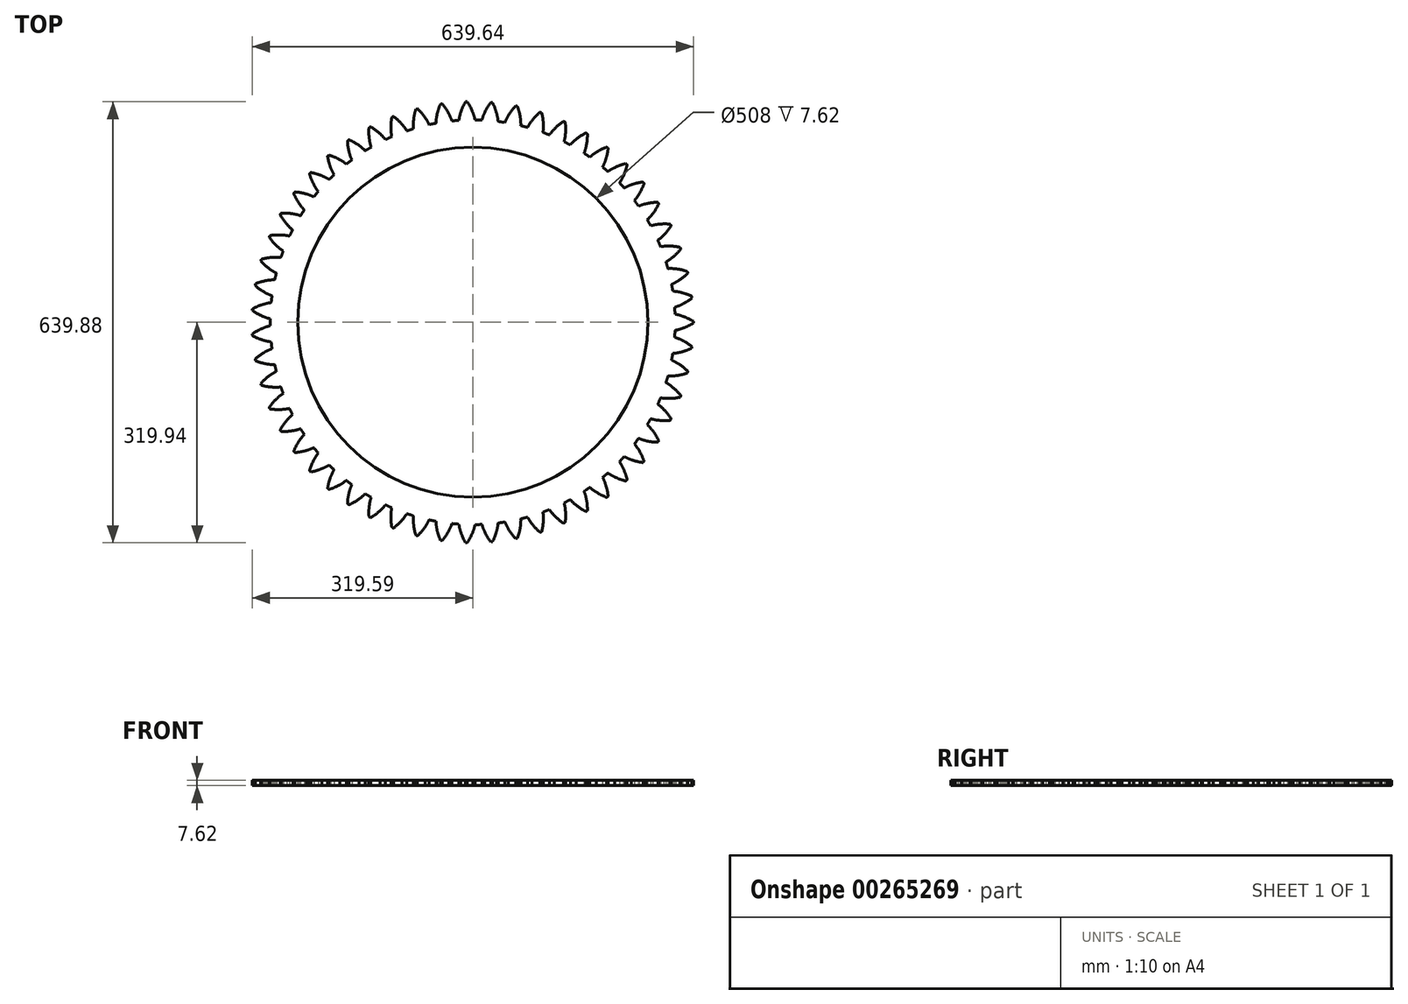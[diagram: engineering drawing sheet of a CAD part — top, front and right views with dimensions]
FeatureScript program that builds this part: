
annotation { "Feature Type Name" : "Feature", "Feature Type Description" : "" }
export const myFeature = defineFeature(function(context is Context, id is Id, definition is map)
    precondition{}
    {
        {
            var Q0;
            Q0=qCreatedBy(makeId("Top.planeOp"),FACE);
            var sketch = newSketch(context, id + "F0", { "sketchPlane" : qUnion([Q0])});
            skCircle(sketch, "E0", {"center": v(0, 0) * mm, "radius": 293.72 * mm});
            skCircle(sketch, "E1", {"center": v(0, 0) * mm, "radius": 304.8 * mm, "construction": true});
            skCircle(sketch, "E2", {"center": v(0, 0) * mm, "radius": 320.04 * mm, "construction": true});
            skLineSegment(sketch, "E3", {"start": v(0, 0) * mm, "end": v(0, 420.14) * mm, "construction": true});
            skLineSegment(sketch, "E4", {"start": v(0, 0) * mm, "end": v(-11.66, 408.27) * mm, "construction": true});
            skLineSegment(sketch, "E5", {"start": v(0, 304.8) * mm, "end": v(-381.83, 304.8) * mm, "construction": true});
            skLineSegment(sketch, "E6", {"start": v(0, 304.8) * mm, "end": v(-397.99, 159.94) * mm, "construction": true});
            skCircle(sketch, "E7", {"center": v(0, 0) * mm, "radius": 286.42 * mm, "construction": true});
            skCircle(sketch, "E8", {"center": v(0, 304.8) * mm, "radius": 76.2 * mm, "construction": true});
            skCircle(sketch, "E9", {"center": v(-71.12, 277.45) * mm, "radius": 76.2 * mm, "construction": true});
            skArc(sketch, "E10", {"start": v(-7.87, 319.94) * mm, "mid": v(-9.14, 319.92) * mm, "end": v(-10.4, 319.87) * mm});
            skArc(sketch, "E11", {"start": v(0, 304.8) * mm, "mid": v(-3.5, 312.6) * mm, "end": v(-7.87, 319.94) * mm});
            skArc(sketch, "E12.MirrorCS", {"start": v(-17.4, 304.3) * mm, "mid": v(-14.35, 312.29) * mm, "end": v(-10.4, 319.87) * mm});
            skArc(sketch, "E13", {"start": v(-17.4, 304.3) * mm, "mid": v(-19.02, 298.73) * mm, "end": v(-20.09, 293.03) * mm});
            skArc(sketch, "E14.MirrorCS", {"start": v(0, 304.8) * mm, "mid": v(1.94, 299.33) * mm, "end": v(3.33, 293.7) * mm});
            skSolve(sketch);
        }
        {
            var Q0;
            Q0=qSketchRegion(id+"F0",true);
            extrude(context, id + "F1", {"entities" : qUnion([Q0]), "depth" : 7.62 * mm});
        }
        {
            var Q0;
            Q0=makeQuery(id+"F1.opExtrude","SWEPT_BODY",BODY,{"disambiguationData":[OSD([sQuery(id+"F0.wireOp",EDGE,"E0"),sQuery(id+"F0.wireOp",EDGE,"91NiUCr4-yXFt-oEsC-2t8w-iLQuIMEs0WGp"),sQuery(id+"F0.wireOp",EDGE,"2eccd6a7-b62e-4e30-96b3-c5b5e07e5a5b0.MirrorCS"),sQuery(id+"F0.wireOp",EDGE,"E10")])]});
            var Q1;
            Q1=makeQuery(id+"F1.opExtrude","SWEPT_FACE",FACE,{"disambiguationData":[OSD([sQuery(id+"F0.wireOp",EDGE,"E0")])]});
            circularPattern(context, id + "F2", {"entities" : qUnion([Q0]), "axis" : qUnion([Q1]), "angle" : 360 * degree, "instanceCount" : 55, "equalSpace" : true});
        }
        {
            var Q0;
            Q0=makeQuery(id+"F1.opExtrude","SWEPT_BODY",BODY,{"disambiguationData":[OSD([sQuery(id+"F0.wireOp",EDGE,"E0"),sQuery(id+"F0.wireOp",EDGE,"E10"),sQuery(id+"F0.wireOp",EDGE,"E11"),sQuery(id+"F0.wireOp",EDGE,"E12.MirrorCS"),sQuery(id+"F0.wireOp",EDGE,"E13"),sQuery(id+"F0.wireOp",EDGE,"E14.MirrorCS")])]});
            var Q1;
            Q1=makeQuery(id+"F2.opPattern","COPY",BODY,{"derivedFrom":makeQuery(id+"F1.opExtrude","SWEPT_BODY",BODY,{"disambiguationData":[OSD([sQuery(id+"F0.wireOp",EDGE,"E0"),sQuery(id+"F0.wireOp",EDGE,"E10"),sQuery(id+"F0.wireOp",EDGE,"E11"),sQuery(id+"F0.wireOp",EDGE,"E12.MirrorCS"),sQuery(id+"F0.wireOp",EDGE,"E13"),sQuery(id+"F0.wireOp",EDGE,"E14.MirrorCS")])]}),"instanceName":"1"});
            var Q2;
            Q2=makeQuery(id+"F2.opPattern","COPY",BODY,{"derivedFrom":makeQuery(id+"F1.opExtrude","SWEPT_BODY",BODY,{"disambiguationData":[OSD([sQuery(id+"F0.wireOp",EDGE,"E0"),sQuery(id+"F0.wireOp",EDGE,"E10"),sQuery(id+"F0.wireOp",EDGE,"E11"),sQuery(id+"F0.wireOp",EDGE,"E12.MirrorCS"),sQuery(id+"F0.wireOp",EDGE,"E13"),sQuery(id+"F0.wireOp",EDGE,"E14.MirrorCS")])]}),"instanceName":"2"});
            var Q3;
            Q3=makeQuery(id+"F2.opPattern","COPY",BODY,{"derivedFrom":makeQuery(id+"F1.opExtrude","SWEPT_BODY",BODY,{"disambiguationData":[OSD([sQuery(id+"F0.wireOp",EDGE,"E0"),sQuery(id+"F0.wireOp",EDGE,"E10"),sQuery(id+"F0.wireOp",EDGE,"E11"),sQuery(id+"F0.wireOp",EDGE,"E12.MirrorCS"),sQuery(id+"F0.wireOp",EDGE,"E13"),sQuery(id+"F0.wireOp",EDGE,"E14.MirrorCS")])]}),"instanceName":"3"});
            var Q4;
            Q4=makeQuery(id+"F2.opPattern","COPY",BODY,{"derivedFrom":makeQuery(id+"F1.opExtrude","SWEPT_BODY",BODY,{"disambiguationData":[OSD([sQuery(id+"F0.wireOp",EDGE,"E0"),sQuery(id+"F0.wireOp",EDGE,"E10"),sQuery(id+"F0.wireOp",EDGE,"E11"),sQuery(id+"F0.wireOp",EDGE,"E12.MirrorCS"),sQuery(id+"F0.wireOp",EDGE,"E13"),sQuery(id+"F0.wireOp",EDGE,"E14.MirrorCS")])]}),"instanceName":"4"});
            var Q5;
            Q5=makeQuery(id+"F2.opPattern","COPY",BODY,{"derivedFrom":makeQuery(id+"F1.opExtrude","SWEPT_BODY",BODY,{"disambiguationData":[OSD([sQuery(id+"F0.wireOp",EDGE,"E0"),sQuery(id+"F0.wireOp",EDGE,"E10"),sQuery(id+"F0.wireOp",EDGE,"E11"),sQuery(id+"F0.wireOp",EDGE,"E12.MirrorCS"),sQuery(id+"F0.wireOp",EDGE,"E13"),sQuery(id+"F0.wireOp",EDGE,"E14.MirrorCS")])]}),"instanceName":"5"});
            var Q6;
            Q6=makeQuery(id+"F2.opPattern","COPY",BODY,{"derivedFrom":makeQuery(id+"F1.opExtrude","SWEPT_BODY",BODY,{"disambiguationData":[OSD([sQuery(id+"F0.wireOp",EDGE,"E0"),sQuery(id+"F0.wireOp",EDGE,"E10"),sQuery(id+"F0.wireOp",EDGE,"E11"),sQuery(id+"F0.wireOp",EDGE,"E12.MirrorCS"),sQuery(id+"F0.wireOp",EDGE,"E13"),sQuery(id+"F0.wireOp",EDGE,"E14.MirrorCS")])]}),"instanceName":"6"});
            var Q7;
            Q7=makeQuery(id+"F2.opPattern","COPY",BODY,{"derivedFrom":makeQuery(id+"F1.opExtrude","SWEPT_BODY",BODY,{"disambiguationData":[OSD([sQuery(id+"F0.wireOp",EDGE,"E0"),sQuery(id+"F0.wireOp",EDGE,"E10"),sQuery(id+"F0.wireOp",EDGE,"E11"),sQuery(id+"F0.wireOp",EDGE,"E12.MirrorCS"),sQuery(id+"F0.wireOp",EDGE,"E13"),sQuery(id+"F0.wireOp",EDGE,"E14.MirrorCS")])]}),"instanceName":"7"});
            var Q8;
            Q8=makeQuery(id+"F2.opPattern","COPY",BODY,{"derivedFrom":makeQuery(id+"F1.opExtrude","SWEPT_BODY",BODY,{"disambiguationData":[OSD([sQuery(id+"F0.wireOp",EDGE,"E0"),sQuery(id+"F0.wireOp",EDGE,"E10"),sQuery(id+"F0.wireOp",EDGE,"E11"),sQuery(id+"F0.wireOp",EDGE,"E12.MirrorCS"),sQuery(id+"F0.wireOp",EDGE,"E13"),sQuery(id+"F0.wireOp",EDGE,"E14.MirrorCS")])]}),"instanceName":"8"});
            var Q9;
            Q9=makeQuery(id+"F2.opPattern","COPY",BODY,{"derivedFrom":makeQuery(id+"F1.opExtrude","SWEPT_BODY",BODY,{"disambiguationData":[OSD([sQuery(id+"F0.wireOp",EDGE,"E0"),sQuery(id+"F0.wireOp",EDGE,"E10"),sQuery(id+"F0.wireOp",EDGE,"E11"),sQuery(id+"F0.wireOp",EDGE,"E12.MirrorCS"),sQuery(id+"F0.wireOp",EDGE,"E13"),sQuery(id+"F0.wireOp",EDGE,"E14.MirrorCS")])]}),"instanceName":"9"});
            var Q10;
            Q10=makeQuery(id+"F2.opPattern","COPY",BODY,{"derivedFrom":makeQuery(id+"F1.opExtrude","SWEPT_BODY",BODY,{"disambiguationData":[OSD([sQuery(id+"F0.wireOp",EDGE,"E0"),sQuery(id+"F0.wireOp",EDGE,"E10"),sQuery(id+"F0.wireOp",EDGE,"E11"),sQuery(id+"F0.wireOp",EDGE,"E12.MirrorCS"),sQuery(id+"F0.wireOp",EDGE,"E13"),sQuery(id+"F0.wireOp",EDGE,"E14.MirrorCS")])]}),"instanceName":"10"});
            var Q11;
            Q11=makeQuery(id+"F2.opPattern","COPY",BODY,{"derivedFrom":makeQuery(id+"F1.opExtrude","SWEPT_BODY",BODY,{"disambiguationData":[OSD([sQuery(id+"F0.wireOp",EDGE,"E0"),sQuery(id+"F0.wireOp",EDGE,"E10"),sQuery(id+"F0.wireOp",EDGE,"E11"),sQuery(id+"F0.wireOp",EDGE,"E12.MirrorCS"),sQuery(id+"F0.wireOp",EDGE,"E13"),sQuery(id+"F0.wireOp",EDGE,"E14.MirrorCS")])]}),"instanceName":"11"});
            var Q12;
            Q12=makeQuery(id+"F2.opPattern","COPY",BODY,{"derivedFrom":makeQuery(id+"F1.opExtrude","SWEPT_BODY",BODY,{"disambiguationData":[OSD([sQuery(id+"F0.wireOp",EDGE,"E0"),sQuery(id+"F0.wireOp",EDGE,"E10"),sQuery(id+"F0.wireOp",EDGE,"E11"),sQuery(id+"F0.wireOp",EDGE,"E12.MirrorCS"),sQuery(id+"F0.wireOp",EDGE,"E13"),sQuery(id+"F0.wireOp",EDGE,"E14.MirrorCS")])]}),"instanceName":"12"});
            var Q13;
            Q13=makeQuery(id+"F2.opPattern","COPY",BODY,{"derivedFrom":makeQuery(id+"F1.opExtrude","SWEPT_BODY",BODY,{"disambiguationData":[OSD([sQuery(id+"F0.wireOp",EDGE,"E0"),sQuery(id+"F0.wireOp",EDGE,"E10"),sQuery(id+"F0.wireOp",EDGE,"E11"),sQuery(id+"F0.wireOp",EDGE,"E12.MirrorCS"),sQuery(id+"F0.wireOp",EDGE,"E13"),sQuery(id+"F0.wireOp",EDGE,"E14.MirrorCS")])]}),"instanceName":"13"});
            var Q14;
            Q14=makeQuery(id+"F2.opPattern","COPY",BODY,{"derivedFrom":makeQuery(id+"F1.opExtrude","SWEPT_BODY",BODY,{"disambiguationData":[OSD([sQuery(id+"F0.wireOp",EDGE,"E0"),sQuery(id+"F0.wireOp",EDGE,"E10"),sQuery(id+"F0.wireOp",EDGE,"E11"),sQuery(id+"F0.wireOp",EDGE,"E12.MirrorCS"),sQuery(id+"F0.wireOp",EDGE,"E13"),sQuery(id+"F0.wireOp",EDGE,"E14.MirrorCS")])]}),"instanceName":"14"});
            var Q15;
            Q15=makeQuery(id+"F2.opPattern","COPY",BODY,{"derivedFrom":makeQuery(id+"F1.opExtrude","SWEPT_BODY",BODY,{"disambiguationData":[OSD([sQuery(id+"F0.wireOp",EDGE,"E0"),sQuery(id+"F0.wireOp",EDGE,"E10"),sQuery(id+"F0.wireOp",EDGE,"E11"),sQuery(id+"F0.wireOp",EDGE,"E12.MirrorCS"),sQuery(id+"F0.wireOp",EDGE,"E13"),sQuery(id+"F0.wireOp",EDGE,"E14.MirrorCS")])]}),"instanceName":"15"});
            var Q16;
            Q16=makeQuery(id+"F2.opPattern","COPY",BODY,{"derivedFrom":makeQuery(id+"F1.opExtrude","SWEPT_BODY",BODY,{"disambiguationData":[OSD([sQuery(id+"F0.wireOp",EDGE,"E0"),sQuery(id+"F0.wireOp",EDGE,"E10"),sQuery(id+"F0.wireOp",EDGE,"E11"),sQuery(id+"F0.wireOp",EDGE,"E12.MirrorCS"),sQuery(id+"F0.wireOp",EDGE,"E13"),sQuery(id+"F0.wireOp",EDGE,"E14.MirrorCS")])]}),"instanceName":"16"});
            var Q17;
            Q17=makeQuery(id+"F2.opPattern","COPY",BODY,{"derivedFrom":makeQuery(id+"F1.opExtrude","SWEPT_BODY",BODY,{"disambiguationData":[OSD([sQuery(id+"F0.wireOp",EDGE,"E0"),sQuery(id+"F0.wireOp",EDGE,"E10"),sQuery(id+"F0.wireOp",EDGE,"E11"),sQuery(id+"F0.wireOp",EDGE,"E12.MirrorCS"),sQuery(id+"F0.wireOp",EDGE,"E13"),sQuery(id+"F0.wireOp",EDGE,"E14.MirrorCS")])]}),"instanceName":"17"});
            var Q18;
            Q18=makeQuery(id+"F2.opPattern","COPY",BODY,{"derivedFrom":makeQuery(id+"F1.opExtrude","SWEPT_BODY",BODY,{"disambiguationData":[OSD([sQuery(id+"F0.wireOp",EDGE,"E0"),sQuery(id+"F0.wireOp",EDGE,"E10"),sQuery(id+"F0.wireOp",EDGE,"E11"),sQuery(id+"F0.wireOp",EDGE,"E12.MirrorCS"),sQuery(id+"F0.wireOp",EDGE,"E13"),sQuery(id+"F0.wireOp",EDGE,"E14.MirrorCS")])]}),"instanceName":"18"});
            var Q19;
            Q19=makeQuery(id+"F2.opPattern","COPY",BODY,{"derivedFrom":makeQuery(id+"F1.opExtrude","SWEPT_BODY",BODY,{"disambiguationData":[OSD([sQuery(id+"F0.wireOp",EDGE,"E0"),sQuery(id+"F0.wireOp",EDGE,"E10"),sQuery(id+"F0.wireOp",EDGE,"E11"),sQuery(id+"F0.wireOp",EDGE,"E12.MirrorCS"),sQuery(id+"F0.wireOp",EDGE,"E13"),sQuery(id+"F0.wireOp",EDGE,"E14.MirrorCS")])]}),"instanceName":"19"});
            var Q20;
            Q20=makeQuery(id+"F2.opPattern","COPY",BODY,{"derivedFrom":makeQuery(id+"F1.opExtrude","SWEPT_BODY",BODY,{"disambiguationData":[OSD([sQuery(id+"F0.wireOp",EDGE,"E0"),sQuery(id+"F0.wireOp",EDGE,"E10"),sQuery(id+"F0.wireOp",EDGE,"E11"),sQuery(id+"F0.wireOp",EDGE,"E12.MirrorCS"),sQuery(id+"F0.wireOp",EDGE,"E13"),sQuery(id+"F0.wireOp",EDGE,"E14.MirrorCS")])]}),"instanceName":"20"});
            var Q21;
            Q21=makeQuery(id+"F2.opPattern","COPY",BODY,{"derivedFrom":makeQuery(id+"F1.opExtrude","SWEPT_BODY",BODY,{"disambiguationData":[OSD([sQuery(id+"F0.wireOp",EDGE,"E0"),sQuery(id+"F0.wireOp",EDGE,"E10"),sQuery(id+"F0.wireOp",EDGE,"E11"),sQuery(id+"F0.wireOp",EDGE,"E12.MirrorCS"),sQuery(id+"F0.wireOp",EDGE,"E13"),sQuery(id+"F0.wireOp",EDGE,"E14.MirrorCS")])]}),"instanceName":"21"});
            var Q22;
            Q22=makeQuery(id+"F2.opPattern","COPY",BODY,{"derivedFrom":makeQuery(id+"F1.opExtrude","SWEPT_BODY",BODY,{"disambiguationData":[OSD([sQuery(id+"F0.wireOp",EDGE,"E0"),sQuery(id+"F0.wireOp",EDGE,"E10"),sQuery(id+"F0.wireOp",EDGE,"E11"),sQuery(id+"F0.wireOp",EDGE,"E12.MirrorCS"),sQuery(id+"F0.wireOp",EDGE,"E13"),sQuery(id+"F0.wireOp",EDGE,"E14.MirrorCS")])]}),"instanceName":"22"});
            var Q23;
            Q23=makeQuery(id+"F2.opPattern","COPY",BODY,{"derivedFrom":makeQuery(id+"F1.opExtrude","SWEPT_BODY",BODY,{"disambiguationData":[OSD([sQuery(id+"F0.wireOp",EDGE,"E0"),sQuery(id+"F0.wireOp",EDGE,"E10"),sQuery(id+"F0.wireOp",EDGE,"E11"),sQuery(id+"F0.wireOp",EDGE,"E12.MirrorCS"),sQuery(id+"F0.wireOp",EDGE,"E13"),sQuery(id+"F0.wireOp",EDGE,"E14.MirrorCS")])]}),"instanceName":"23"});
            var Q24;
            Q24=makeQuery(id+"F2.opPattern","COPY",BODY,{"derivedFrom":makeQuery(id+"F1.opExtrude","SWEPT_BODY",BODY,{"disambiguationData":[OSD([sQuery(id+"F0.wireOp",EDGE,"E0"),sQuery(id+"F0.wireOp",EDGE,"E10"),sQuery(id+"F0.wireOp",EDGE,"E11"),sQuery(id+"F0.wireOp",EDGE,"E12.MirrorCS"),sQuery(id+"F0.wireOp",EDGE,"E13"),sQuery(id+"F0.wireOp",EDGE,"E14.MirrorCS")])]}),"instanceName":"24"});
            var Q25;
            Q25=makeQuery(id+"F2.opPattern","COPY",BODY,{"derivedFrom":makeQuery(id+"F1.opExtrude","SWEPT_BODY",BODY,{"disambiguationData":[OSD([sQuery(id+"F0.wireOp",EDGE,"E0"),sQuery(id+"F0.wireOp",EDGE,"E10"),sQuery(id+"F0.wireOp",EDGE,"E11"),sQuery(id+"F0.wireOp",EDGE,"E12.MirrorCS"),sQuery(id+"F0.wireOp",EDGE,"E13"),sQuery(id+"F0.wireOp",EDGE,"E14.MirrorCS")])]}),"instanceName":"25"});
            var Q26;
            Q26=makeQuery(id+"F2.opPattern","COPY",BODY,{"derivedFrom":makeQuery(id+"F1.opExtrude","SWEPT_BODY",BODY,{"disambiguationData":[OSD([sQuery(id+"F0.wireOp",EDGE,"E0"),sQuery(id+"F0.wireOp",EDGE,"E10"),sQuery(id+"F0.wireOp",EDGE,"E11"),sQuery(id+"F0.wireOp",EDGE,"E12.MirrorCS"),sQuery(id+"F0.wireOp",EDGE,"E13"),sQuery(id+"F0.wireOp",EDGE,"E14.MirrorCS")])]}),"instanceName":"26"});
            var Q27;
            Q27=makeQuery(id+"F2.opPattern","COPY",BODY,{"derivedFrom":makeQuery(id+"F1.opExtrude","SWEPT_BODY",BODY,{"disambiguationData":[OSD([sQuery(id+"F0.wireOp",EDGE,"E0"),sQuery(id+"F0.wireOp",EDGE,"E10"),sQuery(id+"F0.wireOp",EDGE,"E11"),sQuery(id+"F0.wireOp",EDGE,"E12.MirrorCS"),sQuery(id+"F0.wireOp",EDGE,"E13"),sQuery(id+"F0.wireOp",EDGE,"E14.MirrorCS")])]}),"instanceName":"27"});
            var Q28;
            Q28=makeQuery(id+"F2.opPattern","COPY",BODY,{"derivedFrom":makeQuery(id+"F1.opExtrude","SWEPT_BODY",BODY,{"disambiguationData":[OSD([sQuery(id+"F0.wireOp",EDGE,"E0"),sQuery(id+"F0.wireOp",EDGE,"E10"),sQuery(id+"F0.wireOp",EDGE,"E11"),sQuery(id+"F0.wireOp",EDGE,"E12.MirrorCS"),sQuery(id+"F0.wireOp",EDGE,"E13"),sQuery(id+"F0.wireOp",EDGE,"E14.MirrorCS")])]}),"instanceName":"28"});
            var Q29;
            Q29=makeQuery(id+"F2.opPattern","COPY",BODY,{"derivedFrom":makeQuery(id+"F1.opExtrude","SWEPT_BODY",BODY,{"disambiguationData":[OSD([sQuery(id+"F0.wireOp",EDGE,"E0"),sQuery(id+"F0.wireOp",EDGE,"E10"),sQuery(id+"F0.wireOp",EDGE,"E11"),sQuery(id+"F0.wireOp",EDGE,"E12.MirrorCS"),sQuery(id+"F0.wireOp",EDGE,"E13"),sQuery(id+"F0.wireOp",EDGE,"E14.MirrorCS")])]}),"instanceName":"29"});
            var Q30;
            Q30=makeQuery(id+"F2.opPattern","COPY",BODY,{"derivedFrom":makeQuery(id+"F1.opExtrude","SWEPT_BODY",BODY,{"disambiguationData":[OSD([sQuery(id+"F0.wireOp",EDGE,"E0"),sQuery(id+"F0.wireOp",EDGE,"E10"),sQuery(id+"F0.wireOp",EDGE,"E11"),sQuery(id+"F0.wireOp",EDGE,"E12.MirrorCS"),sQuery(id+"F0.wireOp",EDGE,"E13"),sQuery(id+"F0.wireOp",EDGE,"E14.MirrorCS")])]}),"instanceName":"30"});
            var Q31;
            Q31=makeQuery(id+"F2.opPattern","COPY",BODY,{"derivedFrom":makeQuery(id+"F1.opExtrude","SWEPT_BODY",BODY,{"disambiguationData":[OSD([sQuery(id+"F0.wireOp",EDGE,"E0"),sQuery(id+"F0.wireOp",EDGE,"E10"),sQuery(id+"F0.wireOp",EDGE,"E11"),sQuery(id+"F0.wireOp",EDGE,"E12.MirrorCS"),sQuery(id+"F0.wireOp",EDGE,"E13"),sQuery(id+"F0.wireOp",EDGE,"E14.MirrorCS")])]}),"instanceName":"31"});
            var Q32;
            Q32=makeQuery(id+"F2.opPattern","COPY",BODY,{"derivedFrom":makeQuery(id+"F1.opExtrude","SWEPT_BODY",BODY,{"disambiguationData":[OSD([sQuery(id+"F0.wireOp",EDGE,"E0"),sQuery(id+"F0.wireOp",EDGE,"E10"),sQuery(id+"F0.wireOp",EDGE,"E11"),sQuery(id+"F0.wireOp",EDGE,"E12.MirrorCS"),sQuery(id+"F0.wireOp",EDGE,"E13"),sQuery(id+"F0.wireOp",EDGE,"E14.MirrorCS")])]}),"instanceName":"32"});
            var Q33;
            Q33=makeQuery(id+"F2.opPattern","COPY",BODY,{"derivedFrom":makeQuery(id+"F1.opExtrude","SWEPT_BODY",BODY,{"disambiguationData":[OSD([sQuery(id+"F0.wireOp",EDGE,"E0"),sQuery(id+"F0.wireOp",EDGE,"E10"),sQuery(id+"F0.wireOp",EDGE,"E11"),sQuery(id+"F0.wireOp",EDGE,"E12.MirrorCS"),sQuery(id+"F0.wireOp",EDGE,"E13"),sQuery(id+"F0.wireOp",EDGE,"E14.MirrorCS")])]}),"instanceName":"33"});
            var Q34;
            Q34=makeQuery(id+"F2.opPattern","COPY",BODY,{"derivedFrom":makeQuery(id+"F1.opExtrude","SWEPT_BODY",BODY,{"disambiguationData":[OSD([sQuery(id+"F0.wireOp",EDGE,"E0"),sQuery(id+"F0.wireOp",EDGE,"E10"),sQuery(id+"F0.wireOp",EDGE,"E11"),sQuery(id+"F0.wireOp",EDGE,"E12.MirrorCS"),sQuery(id+"F0.wireOp",EDGE,"E13"),sQuery(id+"F0.wireOp",EDGE,"E14.MirrorCS")])]}),"instanceName":"34"});
            var Q35;
            Q35=makeQuery(id+"F2.opPattern","COPY",BODY,{"derivedFrom":makeQuery(id+"F1.opExtrude","SWEPT_BODY",BODY,{"disambiguationData":[OSD([sQuery(id+"F0.wireOp",EDGE,"E0"),sQuery(id+"F0.wireOp",EDGE,"E10"),sQuery(id+"F0.wireOp",EDGE,"E11"),sQuery(id+"F0.wireOp",EDGE,"E12.MirrorCS"),sQuery(id+"F0.wireOp",EDGE,"E13"),sQuery(id+"F0.wireOp",EDGE,"E14.MirrorCS")])]}),"instanceName":"35"});
            var Q36;
            Q36=makeQuery(id+"F2.opPattern","COPY",BODY,{"derivedFrom":makeQuery(id+"F1.opExtrude","SWEPT_BODY",BODY,{"disambiguationData":[OSD([sQuery(id+"F0.wireOp",EDGE,"E0"),sQuery(id+"F0.wireOp",EDGE,"E10"),sQuery(id+"F0.wireOp",EDGE,"E11"),sQuery(id+"F0.wireOp",EDGE,"E12.MirrorCS"),sQuery(id+"F0.wireOp",EDGE,"E13"),sQuery(id+"F0.wireOp",EDGE,"E14.MirrorCS")])]}),"instanceName":"36"});
            var Q37;
            Q37=makeQuery(id+"F2.opPattern","COPY",BODY,{"derivedFrom":makeQuery(id+"F1.opExtrude","SWEPT_BODY",BODY,{"disambiguationData":[OSD([sQuery(id+"F0.wireOp",EDGE,"E0"),sQuery(id+"F0.wireOp",EDGE,"E10"),sQuery(id+"F0.wireOp",EDGE,"E11"),sQuery(id+"F0.wireOp",EDGE,"E12.MirrorCS"),sQuery(id+"F0.wireOp",EDGE,"E13"),sQuery(id+"F0.wireOp",EDGE,"E14.MirrorCS")])]}),"instanceName":"37"});
            var Q38;
            Q38=makeQuery(id+"F2.opPattern","COPY",BODY,{"derivedFrom":makeQuery(id+"F1.opExtrude","SWEPT_BODY",BODY,{"disambiguationData":[OSD([sQuery(id+"F0.wireOp",EDGE,"E0"),sQuery(id+"F0.wireOp",EDGE,"E10"),sQuery(id+"F0.wireOp",EDGE,"E11"),sQuery(id+"F0.wireOp",EDGE,"E12.MirrorCS"),sQuery(id+"F0.wireOp",EDGE,"E13"),sQuery(id+"F0.wireOp",EDGE,"E14.MirrorCS")])]}),"instanceName":"38"});
            var Q39;
            Q39=makeQuery(id+"F2.opPattern","COPY",BODY,{"derivedFrom":makeQuery(id+"F1.opExtrude","SWEPT_BODY",BODY,{"disambiguationData":[OSD([sQuery(id+"F0.wireOp",EDGE,"E0"),sQuery(id+"F0.wireOp",EDGE,"E10"),sQuery(id+"F0.wireOp",EDGE,"E11"),sQuery(id+"F0.wireOp",EDGE,"E12.MirrorCS"),sQuery(id+"F0.wireOp",EDGE,"E13"),sQuery(id+"F0.wireOp",EDGE,"E14.MirrorCS")])]}),"instanceName":"39"});
            var Q40;
            Q40=makeQuery(id+"F2.opPattern","COPY",BODY,{"derivedFrom":makeQuery(id+"F1.opExtrude","SWEPT_BODY",BODY,{"disambiguationData":[OSD([sQuery(id+"F0.wireOp",EDGE,"E0"),sQuery(id+"F0.wireOp",EDGE,"E10"),sQuery(id+"F0.wireOp",EDGE,"E11"),sQuery(id+"F0.wireOp",EDGE,"E12.MirrorCS"),sQuery(id+"F0.wireOp",EDGE,"E13"),sQuery(id+"F0.wireOp",EDGE,"E14.MirrorCS")])]}),"instanceName":"40"});
            var Q41;
            Q41=makeQuery(id+"F2.opPattern","COPY",BODY,{"derivedFrom":makeQuery(id+"F1.opExtrude","SWEPT_BODY",BODY,{"disambiguationData":[OSD([sQuery(id+"F0.wireOp",EDGE,"E0"),sQuery(id+"F0.wireOp",EDGE,"E10"),sQuery(id+"F0.wireOp",EDGE,"E11"),sQuery(id+"F0.wireOp",EDGE,"E12.MirrorCS"),sQuery(id+"F0.wireOp",EDGE,"E13"),sQuery(id+"F0.wireOp",EDGE,"E14.MirrorCS")])]}),"instanceName":"41"});
            var Q42;
            Q42=makeQuery(id+"F2.opPattern","COPY",BODY,{"derivedFrom":makeQuery(id+"F1.opExtrude","SWEPT_BODY",BODY,{"disambiguationData":[OSD([sQuery(id+"F0.wireOp",EDGE,"E0"),sQuery(id+"F0.wireOp",EDGE,"E10"),sQuery(id+"F0.wireOp",EDGE,"E11"),sQuery(id+"F0.wireOp",EDGE,"E12.MirrorCS"),sQuery(id+"F0.wireOp",EDGE,"E13"),sQuery(id+"F0.wireOp",EDGE,"E14.MirrorCS")])]}),"instanceName":"42"});
            var Q43;
            Q43=makeQuery(id+"F2.opPattern","COPY",BODY,{"derivedFrom":makeQuery(id+"F1.opExtrude","SWEPT_BODY",BODY,{"disambiguationData":[OSD([sQuery(id+"F0.wireOp",EDGE,"E0"),sQuery(id+"F0.wireOp",EDGE,"E10"),sQuery(id+"F0.wireOp",EDGE,"E11"),sQuery(id+"F0.wireOp",EDGE,"E12.MirrorCS"),sQuery(id+"F0.wireOp",EDGE,"E13"),sQuery(id+"F0.wireOp",EDGE,"E14.MirrorCS")])]}),"instanceName":"43"});
            var Q44;
            Q44=makeQuery(id+"F2.opPattern","COPY",BODY,{"derivedFrom":makeQuery(id+"F1.opExtrude","SWEPT_BODY",BODY,{"disambiguationData":[OSD([sQuery(id+"F0.wireOp",EDGE,"E0"),sQuery(id+"F0.wireOp",EDGE,"E10"),sQuery(id+"F0.wireOp",EDGE,"E11"),sQuery(id+"F0.wireOp",EDGE,"E12.MirrorCS"),sQuery(id+"F0.wireOp",EDGE,"E13"),sQuery(id+"F0.wireOp",EDGE,"E14.MirrorCS")])]}),"instanceName":"44"});
            var Q45;
            Q45=makeQuery(id+"F2.opPattern","COPY",BODY,{"derivedFrom":makeQuery(id+"F1.opExtrude","SWEPT_BODY",BODY,{"disambiguationData":[OSD([sQuery(id+"F0.wireOp",EDGE,"E0"),sQuery(id+"F0.wireOp",EDGE,"E10"),sQuery(id+"F0.wireOp",EDGE,"E11"),sQuery(id+"F0.wireOp",EDGE,"E12.MirrorCS"),sQuery(id+"F0.wireOp",EDGE,"E13"),sQuery(id+"F0.wireOp",EDGE,"E14.MirrorCS")])]}),"instanceName":"45"});
            var Q46;
            Q46=makeQuery(id+"F2.opPattern","COPY",BODY,{"derivedFrom":makeQuery(id+"F1.opExtrude","SWEPT_BODY",BODY,{"disambiguationData":[OSD([sQuery(id+"F0.wireOp",EDGE,"E0"),sQuery(id+"F0.wireOp",EDGE,"E10"),sQuery(id+"F0.wireOp",EDGE,"E11"),sQuery(id+"F0.wireOp",EDGE,"E12.MirrorCS"),sQuery(id+"F0.wireOp",EDGE,"E13"),sQuery(id+"F0.wireOp",EDGE,"E14.MirrorCS")])]}),"instanceName":"46"});
            var Q47;
            Q47=makeQuery(id+"F2.opPattern","COPY",BODY,{"derivedFrom":makeQuery(id+"F1.opExtrude","SWEPT_BODY",BODY,{"disambiguationData":[OSD([sQuery(id+"F0.wireOp",EDGE,"E0"),sQuery(id+"F0.wireOp",EDGE,"E10"),sQuery(id+"F0.wireOp",EDGE,"E11"),sQuery(id+"F0.wireOp",EDGE,"E12.MirrorCS"),sQuery(id+"F0.wireOp",EDGE,"E13"),sQuery(id+"F0.wireOp",EDGE,"E14.MirrorCS")])]}),"instanceName":"47"});
            var Q48;
            Q48=makeQuery(id+"F2.opPattern","COPY",BODY,{"derivedFrom":makeQuery(id+"F1.opExtrude","SWEPT_BODY",BODY,{"disambiguationData":[OSD([sQuery(id+"F0.wireOp",EDGE,"E0"),sQuery(id+"F0.wireOp",EDGE,"E10"),sQuery(id+"F0.wireOp",EDGE,"E11"),sQuery(id+"F0.wireOp",EDGE,"E12.MirrorCS"),sQuery(id+"F0.wireOp",EDGE,"E13"),sQuery(id+"F0.wireOp",EDGE,"E14.MirrorCS")])]}),"instanceName":"48"});
            var Q49;
            Q49=makeQuery(id+"F2.opPattern","COPY",BODY,{"derivedFrom":makeQuery(id+"F1.opExtrude","SWEPT_BODY",BODY,{"disambiguationData":[OSD([sQuery(id+"F0.wireOp",EDGE,"E0"),sQuery(id+"F0.wireOp",EDGE,"E10"),sQuery(id+"F0.wireOp",EDGE,"E11"),sQuery(id+"F0.wireOp",EDGE,"E12.MirrorCS"),sQuery(id+"F0.wireOp",EDGE,"E13"),sQuery(id+"F0.wireOp",EDGE,"E14.MirrorCS")])]}),"instanceName":"49"});
            var Q50;
            Q50=makeQuery(id+"F2.opPattern","COPY",BODY,{"derivedFrom":makeQuery(id+"F1.opExtrude","SWEPT_BODY",BODY,{"disambiguationData":[OSD([sQuery(id+"F0.wireOp",EDGE,"E0"),sQuery(id+"F0.wireOp",EDGE,"E10"),sQuery(id+"F0.wireOp",EDGE,"E11"),sQuery(id+"F0.wireOp",EDGE,"E12.MirrorCS"),sQuery(id+"F0.wireOp",EDGE,"E13"),sQuery(id+"F0.wireOp",EDGE,"E14.MirrorCS")])]}),"instanceName":"50"});
            var Q51;
            Q51=makeQuery(id+"F2.opPattern","COPY",BODY,{"derivedFrom":makeQuery(id+"F1.opExtrude","SWEPT_BODY",BODY,{"disambiguationData":[OSD([sQuery(id+"F0.wireOp",EDGE,"E0"),sQuery(id+"F0.wireOp",EDGE,"E10"),sQuery(id+"F0.wireOp",EDGE,"E11"),sQuery(id+"F0.wireOp",EDGE,"E12.MirrorCS"),sQuery(id+"F0.wireOp",EDGE,"E13"),sQuery(id+"F0.wireOp",EDGE,"E14.MirrorCS")])]}),"instanceName":"51"});
            var Q52;
            Q52=makeQuery(id+"F2.opPattern","COPY",BODY,{"derivedFrom":makeQuery(id+"F1.opExtrude","SWEPT_BODY",BODY,{"disambiguationData":[OSD([sQuery(id+"F0.wireOp",EDGE,"E0"),sQuery(id+"F0.wireOp",EDGE,"E10"),sQuery(id+"F0.wireOp",EDGE,"E11"),sQuery(id+"F0.wireOp",EDGE,"E12.MirrorCS"),sQuery(id+"F0.wireOp",EDGE,"E13"),sQuery(id+"F0.wireOp",EDGE,"E14.MirrorCS")])]}),"instanceName":"52"});
            var Q53;
            Q53=makeQuery(id+"F2.opPattern","COPY",BODY,{"derivedFrom":makeQuery(id+"F1.opExtrude","SWEPT_BODY",BODY,{"disambiguationData":[OSD([sQuery(id+"F0.wireOp",EDGE,"E0"),sQuery(id+"F0.wireOp",EDGE,"E10"),sQuery(id+"F0.wireOp",EDGE,"E11"),sQuery(id+"F0.wireOp",EDGE,"E12.MirrorCS"),sQuery(id+"F0.wireOp",EDGE,"E13"),sQuery(id+"F0.wireOp",EDGE,"E14.MirrorCS")])]}),"instanceName":"53"});
            var Q54;
            Q54=makeQuery(id+"F2.opPattern","COPY",BODY,{"derivedFrom":makeQuery(id+"F1.opExtrude","SWEPT_BODY",BODY,{"disambiguationData":[OSD([sQuery(id+"F0.wireOp",EDGE,"E0"),sQuery(id+"F0.wireOp",EDGE,"E10"),sQuery(id+"F0.wireOp",EDGE,"E11"),sQuery(id+"F0.wireOp",EDGE,"E12.MirrorCS"),sQuery(id+"F0.wireOp",EDGE,"E13"),sQuery(id+"F0.wireOp",EDGE,"E14.MirrorCS")])]}),"instanceName":"54"});
            booleanBodies(context, id + "F3", {"operationType" : BooleanOperationType.UNION, "tools" : qUnion([Q0, Q1, Q2, Q3, Q4, Q5, Q6, Q7, Q8, Q9, Q10, Q11, Q12, Q13, Q14, Q15, Q16, Q17, Q18, Q19, Q20, Q21, Q22, Q23, Q24, Q25, Q26, Q27, Q28, Q29, Q30, Q31, Q32, Q33, Q34, Q35, Q36, Q37, Q38, Q39, Q40, Q41, Q42, Q43, Q44, Q45, Q46, Q47, Q48, Q49, Q50, Q51, Q52, Q53, Q54])});
        }
        {
            var Q0;
            {var subQ0=makeQuery(id+"F1.opExtrude","CAP_FACE",FACE,{"disambiguationData":[OSD([sQuery(id+"F0.wireOp",EDGE,"E0"),sQuery(id+"F0.wireOp",EDGE,"E10"),sQuery(id+"F0.wireOp",EDGE,"E11"),sQuery(id+"F0.wireOp",EDGE,"E12.MirrorCS"),sQuery(id+"F0.wireOp",EDGE,"E13"),sQuery(id+"F0.wireOp",EDGE,"E14.MirrorCS")])],"isStart":false});Q0=makeQuery(id+"F3.opBoolean","MERGE",FACE,{"derivedFrom":[subQ0,makeQuery(id+"F2.opPattern","COPY",FACE,{"derivedFrom":subQ0,"instanceName":"1"}),makeQuery(id+"F2.opPattern","COPY",FACE,{"derivedFrom":subQ0,"instanceName":"2"}),makeQuery(id+"F2.opPattern","COPY",FACE,{"derivedFrom":subQ0,"instanceName":"3"}),makeQuery(id+"F2.opPattern","COPY",FACE,{"derivedFrom":subQ0,"instanceName":"4"}),makeQuery(id+"F2.opPattern","COPY",FACE,{"derivedFrom":subQ0,"instanceName":"5"}),makeQuery(id+"F2.opPattern","COPY",FACE,{"derivedFrom":subQ0,"instanceName":"6"}),makeQuery(id+"F2.opPattern","COPY",FACE,{"derivedFrom":subQ0,"instanceName":"7"}),makeQuery(id+"F2.opPattern","COPY",FACE,{"derivedFrom":subQ0,"instanceName":"8"}),makeQuery(id+"F2.opPattern","COPY",FACE,{"derivedFrom":subQ0,"instanceName":"9"}),makeQuery(id+"F2.opPattern","COPY",FACE,{"derivedFrom":subQ0,"instanceName":"10"}),makeQuery(id+"F2.opPattern","COPY",FACE,{"derivedFrom":subQ0,"instanceName":"11"}),makeQuery(id+"F2.opPattern","COPY",FACE,{"derivedFrom":subQ0,"instanceName":"12"}),makeQuery(id+"F2.opPattern","COPY",FACE,{"derivedFrom":subQ0,"instanceName":"13"}),makeQuery(id+"F2.opPattern","COPY",FACE,{"derivedFrom":subQ0,"instanceName":"14"}),makeQuery(id+"F2.opPattern","COPY",FACE,{"derivedFrom":subQ0,"instanceName":"15"}),makeQuery(id+"F2.opPattern","COPY",FACE,{"derivedFrom":subQ0,"instanceName":"16"}),makeQuery(id+"F2.opPattern","COPY",FACE,{"derivedFrom":subQ0,"instanceName":"17"}),makeQuery(id+"F2.opPattern","COPY",FACE,{"derivedFrom":subQ0,"instanceName":"18"}),makeQuery(id+"F2.opPattern","COPY",FACE,{"derivedFrom":subQ0,"instanceName":"19"}),makeQuery(id+"F2.opPattern","COPY",FACE,{"derivedFrom":subQ0,"instanceName":"20"}),makeQuery(id+"F2.opPattern","COPY",FACE,{"derivedFrom":subQ0,"instanceName":"21"}),makeQuery(id+"F2.opPattern","COPY",FACE,{"derivedFrom":subQ0,"instanceName":"22"}),makeQuery(id+"F2.opPattern","COPY",FACE,{"derivedFrom":subQ0,"instanceName":"23"}),makeQuery(id+"F2.opPattern","COPY",FACE,{"derivedFrom":subQ0,"instanceName":"24"}),makeQuery(id+"F2.opPattern","COPY",FACE,{"derivedFrom":subQ0,"instanceName":"25"}),makeQuery(id+"F2.opPattern","COPY",FACE,{"derivedFrom":subQ0,"instanceName":"26"}),makeQuery(id+"F2.opPattern","COPY",FACE,{"derivedFrom":subQ0,"instanceName":"27"}),makeQuery(id+"F2.opPattern","COPY",FACE,{"derivedFrom":subQ0,"instanceName":"28"}),makeQuery(id+"F2.opPattern","COPY",FACE,{"derivedFrom":subQ0,"instanceName":"29"}),makeQuery(id+"F2.opPattern","COPY",FACE,{"derivedFrom":subQ0,"instanceName":"30"}),makeQuery(id+"F2.opPattern","COPY",FACE,{"derivedFrom":subQ0,"instanceName":"31"}),makeQuery(id+"F2.opPattern","COPY",FACE,{"derivedFrom":subQ0,"instanceName":"32"}),makeQuery(id+"F2.opPattern","COPY",FACE,{"derivedFrom":subQ0,"instanceName":"33"}),makeQuery(id+"F2.opPattern","COPY",FACE,{"derivedFrom":subQ0,"instanceName":"34"}),makeQuery(id+"F2.opPattern","COPY",FACE,{"derivedFrom":subQ0,"instanceName":"35"}),makeQuery(id+"F2.opPattern","COPY",FACE,{"derivedFrom":subQ0,"instanceName":"36"}),makeQuery(id+"F2.opPattern","COPY",FACE,{"derivedFrom":subQ0,"instanceName":"37"}),makeQuery(id+"F2.opPattern","COPY",FACE,{"derivedFrom":subQ0,"instanceName":"38"}),makeQuery(id+"F2.opPattern","COPY",FACE,{"derivedFrom":subQ0,"instanceName":"39"}),makeQuery(id+"F2.opPattern","COPY",FACE,{"derivedFrom":subQ0,"instanceName":"40"}),makeQuery(id+"F2.opPattern","COPY",FACE,{"derivedFrom":subQ0,"instanceName":"41"}),makeQuery(id+"F2.opPattern","COPY",FACE,{"derivedFrom":subQ0,"instanceName":"42"}),makeQuery(id+"F2.opPattern","COPY",FACE,{"derivedFrom":subQ0,"instanceName":"43"}),makeQuery(id+"F2.opPattern","COPY",FACE,{"derivedFrom":subQ0,"instanceName":"44"}),makeQuery(id+"F2.opPattern","COPY",FACE,{"derivedFrom":subQ0,"instanceName":"45"}),makeQuery(id+"F2.opPattern","COPY",FACE,{"derivedFrom":subQ0,"instanceName":"46"}),makeQuery(id+"F2.opPattern","COPY",FACE,{"derivedFrom":subQ0,"instanceName":"47"}),makeQuery(id+"F2.opPattern","COPY",FACE,{"derivedFrom":subQ0,"instanceName":"48"}),makeQuery(id+"F2.opPattern","COPY",FACE,{"derivedFrom":subQ0,"instanceName":"49"}),makeQuery(id+"F2.opPattern","COPY",FACE,{"derivedFrom":subQ0,"instanceName":"50"}),makeQuery(id+"F2.opPattern","COPY",FACE,{"derivedFrom":subQ0,"instanceName":"51"}),makeQuery(id+"F2.opPattern","COPY",FACE,{"derivedFrom":subQ0,"instanceName":"52"}),makeQuery(id+"F2.opPattern","COPY",FACE,{"derivedFrom":subQ0,"instanceName":"53"}),makeQuery(id+"F2.opPattern","COPY",FACE,{"derivedFrom":subQ0,"instanceName":"54"})]});}
            var sketch = newSketch(context, id + "F4", { "sketchPlane" : qUnion([Q0])});
            skCircle(sketch, "E15", {"center": v(0, 0) * mm, "radius": 254 * mm});
            skSolve(sketch);
        }
        {
            var Q0;
            Q0 = qSketchRegion(id + "F4", true);
            extrude(context, id + "F5", {"entities" : qUnion([Q0]), "operationType" : NewBodyOperationType.REMOVE, "oppositeDirection" : true, "depth" : 25.4 * mm});
        }
    });
